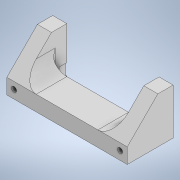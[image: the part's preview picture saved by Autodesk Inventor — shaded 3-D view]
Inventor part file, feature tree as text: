
AUTODESK INVENTOR PART (.ipt)
format: ipt  version: 2021 (Build 250183000, 183)  size: 625,664 bytes
history: native  units: in
note: dims shown in document units (in); Inventor stores cm internally (conversion verified against a paired STEP export)
features: projected_geometry x9, sketch x8, extrude x7, mirror x4, pattern_linear x3, fillet x2, chamfer x2, hole x1
ambient origin geometry x8: Origin, YZ Plane, XZ Plane, XY Plane, X Axis, Y Axis, Z Axis, Center Point
bodies: Solid1 (feature_tree)
feature tree (36):
  extrude  "Extrusion1"  Depth=0.5in
  extrude  "Extrusion2"  Depth=0.46in
  mirror  "Mirror1"
  fillet  "Fillet1"  Radius=0.5in
  extrude  "Extrusion3"  Depth=0.162in
  pattern_linear  "Rectangular Pattern1"  Count1=11 Spacing1=0.25in
  extrude  "Extrusion4"  Depth=0.375in
  mirror  "Mirror2"
  hole  "Hole1"  [1 undecoded]
  mirror  "Mirror3"
  extrude  "Extrusion5"  Depth=0.05in
  chamfer  "Chamfer2"  Distance=0.236in
  fillet  "Fillet3"  Radius=0.8108in
  chamfer  "Chamfer3"  Distance=1.0in
  extrude  "Extrusion6"  Depth=1.0in TaperAngle=45.0deg
  pattern_linear  "Rectangular Pattern2"  Spacing1=0.5in  [1 undecoded]
  extrude  "Extrusion7"  Depth=0.05in TaperAngle=45.0deg
  pattern_linear  "Rectangular Pattern3"  Spacing1=0.125in  [1 undecoded]
  mirror  "Mirror4"
  sketch  "Sketch1"  dims[d0=3.938in d1=0.5in]
  sketch  "Sketch2"  dims[d2=1.0in d3=0.0in d4=0.46in d5=0.5in d6=0.0in]
  projected_geometry  "Projected Loop1"
  sketch  "Sketch3"  dims[d7=0.125in d9=0.162in]
  projected_geometry  "Projected Loop2"
  sketch  "Sketch4"  dims[d10=0.087in]
  projected_geometry  "Projected Loop3"
  projected_geometry  "Projected Loop4"
  sketch  "Sketch5"  dims[d11=0.0625in d12=0.0in d13=4.3307in d15=0.25in]
  projected_geometry  "Projected Loop5"
  projected_geometry  "Projected Loop6"
  sketch  "Sketch6"  dims[d19=0.04in d20=0.375in]
  projected_geometry  "Projected Loop7"
  sketch  "Sketch7"  dims[d21=0.02in d22=0.25in d23=0.0in]
  projected_geometry  "Projected Loop8"
  sketch  "Sketch8"  dims[d24=0.266in d25=0.276in d26=0.236in d27=0.17in d28=0.75in d29=0.507in d30=0.25in d31=0.5635in d32=0.12in d33=0.8108in d34=1.0in d35=0.0in d36=1.0in d37=0.125in d38=45.0deg d39=0.5in d41=0.01in d42=0.125in d43=45.0deg d44=0.125in d45=0.175in d46=0.025in d47=0.0in d48=7.4803in d50=0.185in d51=1.9685in d53=0.185in d54=0.125in d55=0.15in d56=0.05in d57=0.0in d58=1.1811in d60=0.15in d61=0.7874in d63=0.15in]
  projected_geometry  "Projected Loop9"
note: 3 required parameter values undecoded (feature->parameter linkage not recoverable at this tier; creation-order binding heuristic only, values carry confidence <= 0.55)
